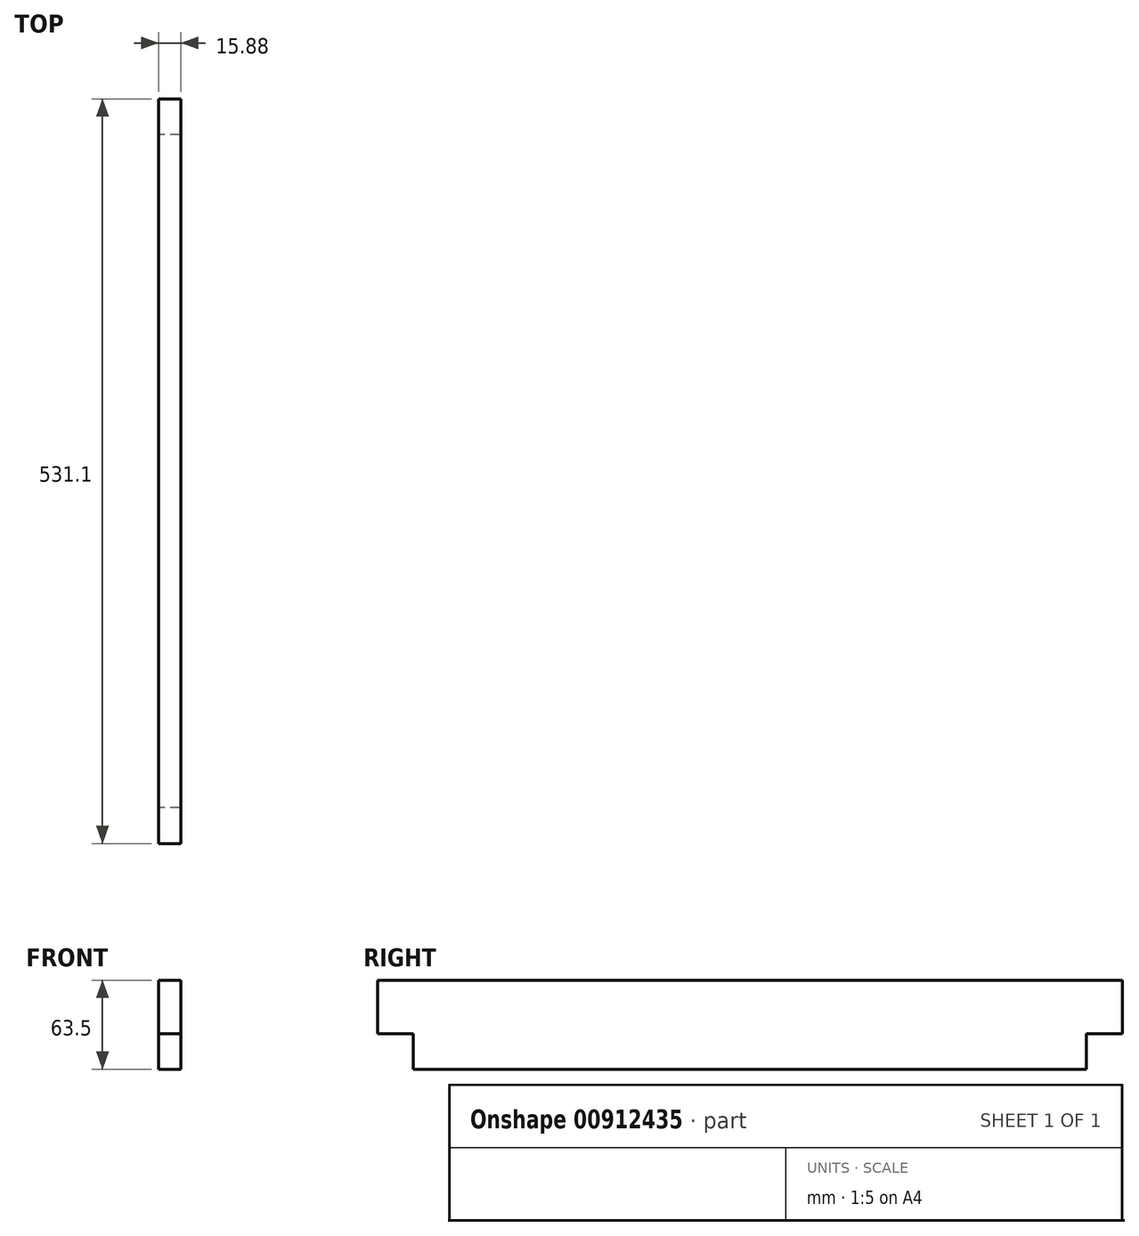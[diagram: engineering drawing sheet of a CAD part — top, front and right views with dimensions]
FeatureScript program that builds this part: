
annotation { "Feature Type Name" : "Feature", "Feature Type Description" : "" }
export const myFeature = defineFeature(function(context is Context, id is Id, definition is map)
    precondition{}
    {
        {
            var Q0;
            Q0=qCreatedBy(makeId("Right.planeOp"),FACE);
            var sketch = newSketch(context, id + "F0", { "sketchPlane" : qUnion([Q0])});
            skLineSegment(sketch, "E0", {"start": v(0, 0) * mm, "end": v(0, 25.4) * mm});
            skLineSegment(sketch, "E1", {"start": v(0, 25.4) * mm, "end": v(-25.55, 25.4) * mm});
            skLineSegment(sketch, "E2", {"start": v(-25.55, 25.4) * mm, "end": v(-25.55, 63.5) * mm});
            skLineSegment(sketch, "E3", {"start": v(-25.55, 63.5) * mm, "end": v(505.55, 63.5) * mm});
            skLineSegment(sketch, "E4", {"start": v(505.55, 63.5) * mm, "end": v(505.55, 25.4) * mm});
            skLineSegment(sketch, "E5", {"start": v(505.55, 25.4) * mm, "end": v(480, 25.4) * mm});
            skLineSegment(sketch, "E6", {"start": v(480, 25.4) * mm, "end": v(480, 0) * mm});
            skLineSegment(sketch, "E7", {"start": v(480, 0) * mm, "end": v(0, 0) * mm});
            skSolve(sketch);
        }
        {
            var Q0;
            Q0 = qSketchRegion(id + "F0", true);
            extrude(context, id + "F1", {"entities" : qUnion([Q0]), "depth" : 15.88 * mm, "offsetDistance" : 25 * mm});
        }
    });
